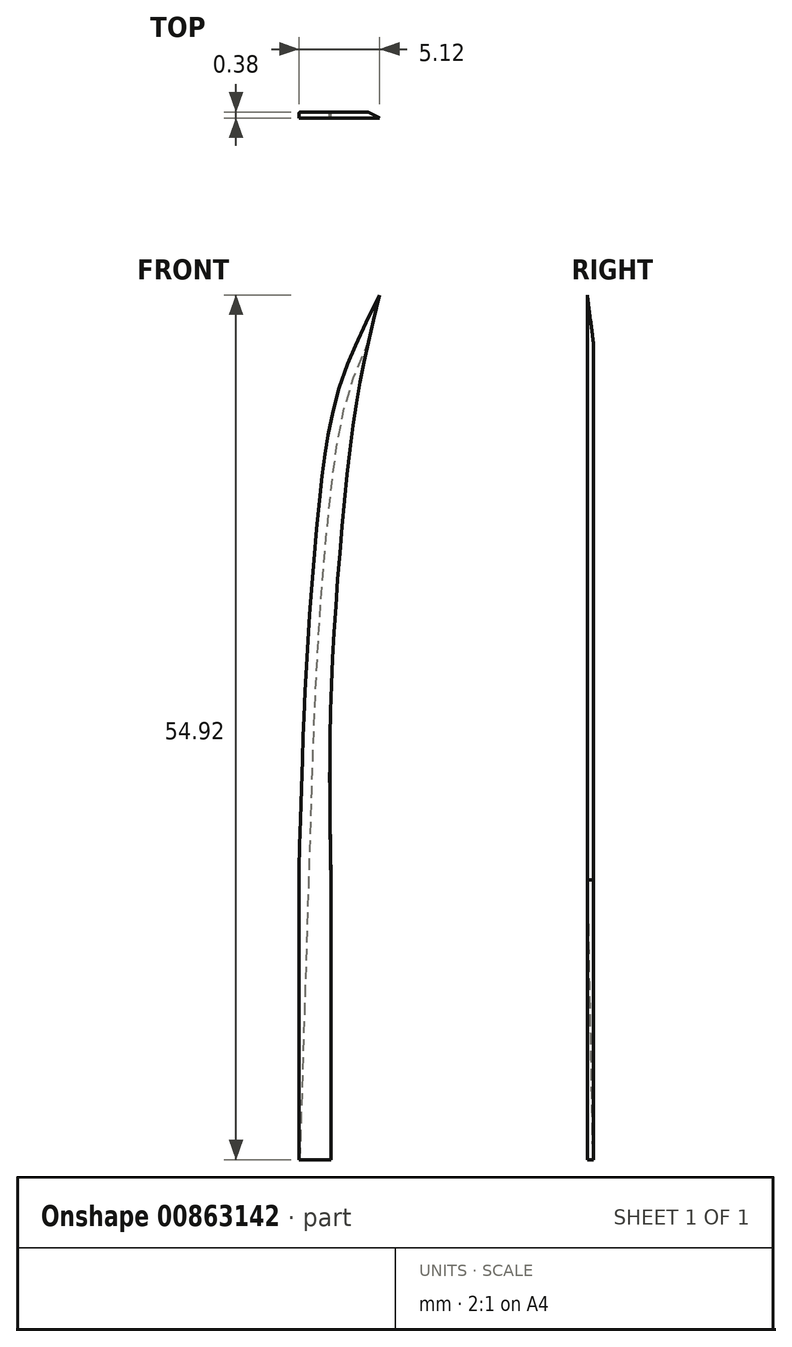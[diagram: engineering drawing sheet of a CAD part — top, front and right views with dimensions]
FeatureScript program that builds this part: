
annotation { "Feature Type Name" : "Feature", "Feature Type Description" : "" }
export const myFeature = defineFeature(function(context is Context, id is Id, definition is map)
    precondition{}
    {
        {
            var Q0;
            Q0=qCreatedBy(makeId("Front.planeOp"),FACE);
            var sketch = newSketch(context, id + "F0", { "sketchPlane" : qUnion([Q0])});
            skLineSegment(sketch, "E0", {"start": v(0, 0) * mm, "end": v(2.03, 0) * mm});
            skLineSegment(sketch, "E1", {"start": v(0, 0) * mm, "end": v(0, 25.4) * mm});
            skLineSegment(sketch, "E2", {"start": v(2.03, 0) * mm, "end": v(2.03, 17.78) * mm});
            skFitSpline(sketch, "E3", {"points": [v(2.03, 17.78) * mm, v(2.03, 29.24) * mm, v(2.67, 39.46) * mm, v(3.7, 48.44) * mm, v(5.36, 55.88) * mm], "startDerivative": vector(-0.98, 47.6) * mm, "endDerivative": vector(10.63, 43.43) * mm});
            skFitSpline(sketch, "E4", {"points": [v(0, 25.4) * mm, v(1.02, 41.31) * mm, v(2.16, 48.44) * mm, v(5.36, 55.88) * mm], "startDerivative": vector(1.39, 44.06) * mm, "endDerivative": vector(17.91, 35.67) * mm});
            skSolve(sketch);
        }
        {
            var Q0;
            Q0=makeQuery(id+"F0.imprint","IMPRINT",FACE,{"disambiguationData":[TD([[makeQuery(id+"F0.imprint","IMPRINT",EDGE,{"derivedFrom":sQuery(id+"F0.wireOp",EDGE,"E0")}),1.0]])]});
            extrude(context, id + "F1", {"entities" : qUnion([Q0]), "depth" : 0.38 * mm, "offsetDistance" : 25.4 * mm});
        }
        {
            var Q0;
            Q0=makeQuery(id+"F1.opExtrude","CAP_EDGE",EDGE,{"disambiguationData":[OSD([sQuery(id+"F0.wireOp",EDGE,"E4")])],"isStart":true});
            chamfer(context, id + "F2", {"entities" : qUnion([Q0]), "chamferType" : ChamferType.OFFSET_ANGLE, "width" : 0.5 * mm, "oppositeDirection" : true, "angle" : 60 * degree, "tangentPropagation" : true});
        }
    });
